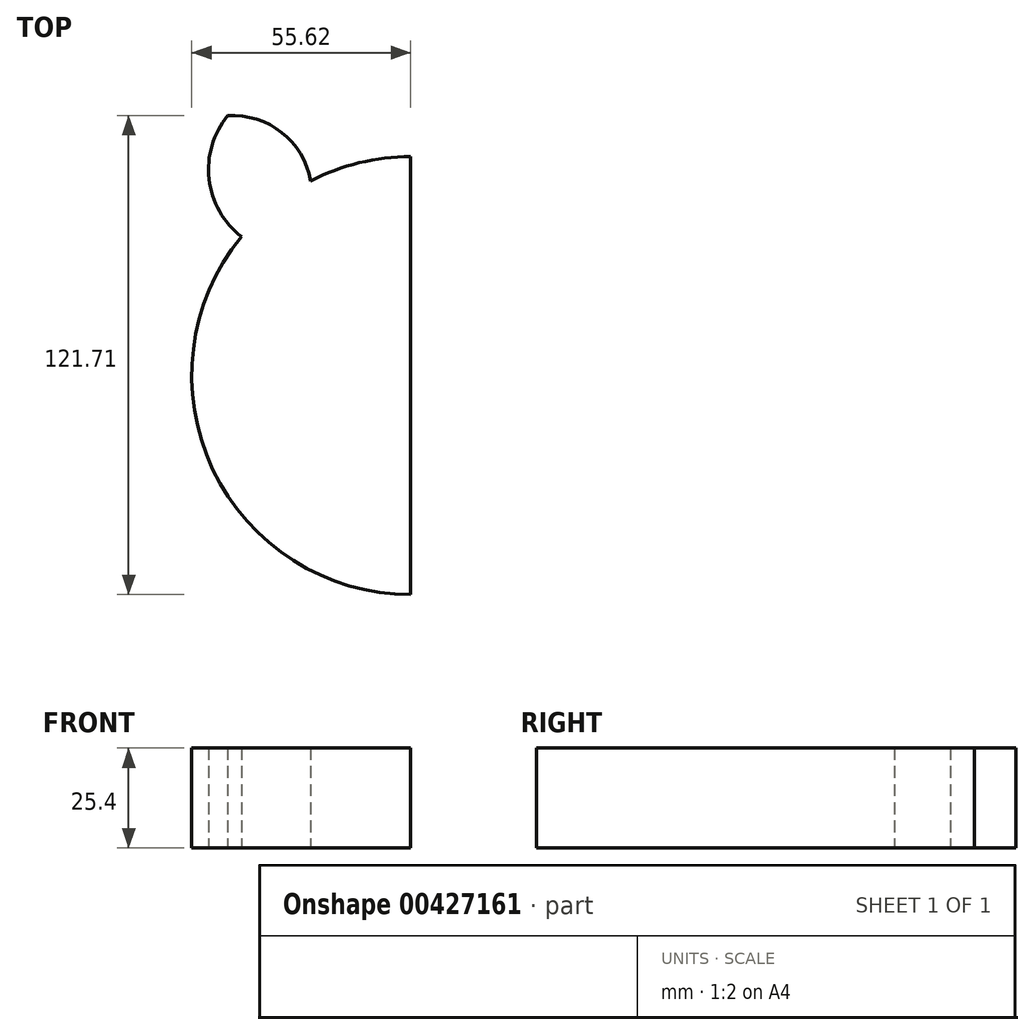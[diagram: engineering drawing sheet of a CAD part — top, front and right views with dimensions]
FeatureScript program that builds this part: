
annotation { "Feature Type Name" : "Feature", "Feature Type Description" : "" }
export const myFeature = defineFeature(function(context is Context, id is Id, definition is map)
    precondition{}
    {
        {
            var Q0;
            Q0=qCreatedBy(makeId("Top.planeOp"),FACE);
            var sketch = newSketch(context, id + "F0", { "sketchPlane" : qUnion([Q0])});
            skArc(sketch, "E0", {"start": v(0, 55.62) * mm, "mid": v(-55.62, 0) * mm, "end": v(0, -55.62) * mm});
            skArc(sketch, "E1", {"start": v(-46.45, 66.05) * mm, "mid": v(-51.23, 49.93) * mm, "end": v(-43, 35.27) * mm});
            skArc(sketch, "E2", {"start": v(-25.4, 49.49) * mm, "mid": v(-32.77, 61.78) * mm, "end": v(-46.45, 66.05) * mm});
            skLineSegment(sketch, "E3", {"start": v(0, 0) * mm, "end": v(0, -55.62) * mm});
            skLineSegment(sketch, "E4", {"start": v(0, -55.62) * mm, "end": v(0, 55.62) * mm});
            skPoint(sketch, "E5.start.orphan", {"position": v(87, 55.62) * mm});
            skPoint(sketch, "E6.orphan", {"position": v(80, 0) * mm});
            skPoint(sketch, "E7.trimOffspring.end.orphan", {"position": v(0, -58.26) * mm});
            skSolve(sketch);
        }
        {
            var Q0;
            Q0 = qSketchRegion(id + "F0", true);
            extrude(context, id + "F1", {"entities" : qUnion([Q0]), "depth" : 25.4 * mm});
        }
    });
